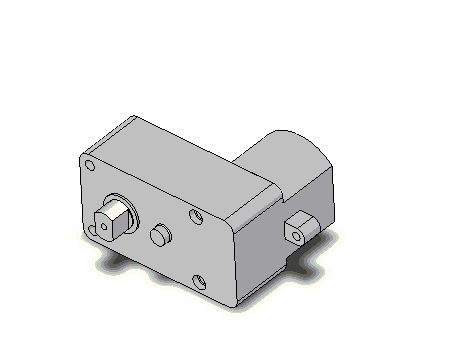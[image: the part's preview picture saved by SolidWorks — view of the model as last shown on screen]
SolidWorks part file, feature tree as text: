
SOLIDWORKS PART (.sldprt)
format: sldprt  version: not decoded by parser v0  size: 541,184 bytes
history: native  units: mm
features: sketch x16, extrude x8, plane x5, cut_extrude x5, chamfer x2, material x1, mirror x1 + 1 further entry (+11 scaffold rows collapsed)
feature tree (50):
  scaffold x11  (default folders/planes/origin — collapsed)
  material  "Material <not specified>"
  "Annotations"  RD1=4.445mm RD3=2mm RD2=2.286mm
  sketch  "Sketch1"  dims[c1.D3=2.5mm c1.D4=5.0mm c1.D6=2.5mm c1.D1=41.8mm c1.D2=22.7mm c2.D4=~40.298183mm c2.D5=21.2mm]
  extrude  "Base-Extrude"  Depth=15.8115mm
  sketch  "Sketch2"  dims[c1.D1=~4.28035mm c1.D2=9.271mm c1.D3=1.75mm c1.D4=3.5mm c2.D1=15.6mm c2.D4=~11.04392mm]
  extrude  "Boss-Extrude1"  Depth=0.55mm
  sketch  "Sketch3"  dims[D1=6.985mm D2=1.5mm]
  extrude  "Boss-Extrude2"  Depth=5.842mm
  plane  "Plane1"  Offset=5.08mm
  sketch  "Sketch5"  dims[D1=3.5mm D2=4.7752mm D3=2.3876mm]
  cut_extrude  "Cut-Extrude1"  [1 undecoded]
  sketch  "Sketch6"  dims[c1.D1=~1.372138mm c1.D2=3.937mm c2.D1=24.257mm]
  extrude  "Boss-Extrude3"  Depth=2mm
  plane  "Backside Plane"  Offset=0mm
  sketch  "Sketch8"
  plane  "Middle Plane"
  sketch  "Sketch11"  dims[c1.D1=7.2mm c1.D2=9.525mm c1.D3=6.9088mm c2.D1=~11.04392mm]
  extrude  "Boss-Extrude4"  Depth=2.794mm
  sketch  "Sketch12"  dims[D1=6.9088mm]
  extrude  "Boss-Extrude5"  Depth=6.731mm
  sketch  "Sketch15"  dims[c1.D2=~12.270569mm c1.D1=17.4mm c2.D1=15.66mm c2.D5=1.15mm c2.D6=1.0mm c2.D7=5.0mm]
  sketch  "Sketch16"  dims[c1.D1=~1.040407mm c1.D2=~0.973054mm c1.D5=2.0mm c2.D2=2.286mm c2.D1=2.0mm c2.D3=2.286mm c3.D1=5.334mm c3.D2=3.3mm c3.D3=4.572mm c3.D4=11.35mm c3.D5=11.35mm c4.D1=5.205mm c4.D2=3.3mm c4.D3=3.3mm c4.D4=3.3mm c5.D2=3.175mm]
  extrude  "Boss-Extrude7"  Depth=5.08mm
  sketch  "Sketch18"
  plane  "Plane5"
  mirror  "Mirror2"
  sketch  "Sketch33"
  sketch  "Sketch34"
  extrude  "Extrude1"  Depth=4.445mm
  sketch  "Sketch35"  dims[D1=6.096mm D2=11.35mm D3=7.55mm D4=7.55mm]
  cut_extrude  "Cut-Extrude4"  Depth=14.445mm
  cut_extrude  "Cut-Extrude5"  Depth=10mm
  chamfer  "Chamfer1"  Distance=0.25mm Angle=45deg
  chamfer  "Chamfer2"  Distance=0.25mm Angle=45deg
  sketch  "Sketch36"  dims[c1.D1=3.5mm c1.D2=3.5mm c2.D1=3.5mm c2.D2=~0.070127mm]
  cut_extrude  "Cut-Extrude6"  Depth=1.525mm
  plane  "Plane6"  Offset=4.191mm
  sketch  "Sketch38"  dims[c1.D2=6.9088mm c1.D1=4.699mm c2.D2=2.3495mm]
  cut_extrude  "Cut-Extrude7"  [1 undecoded]
decode coverage: 25 of 32 modeling features carry decoded parameters; 1 rows unclassified (native names shown)
note: ~ marks probable driven/reference dimensions
note: 2 parameter values undecoded
note: suppression state not decoded; provenance and decode notes live in map.json
